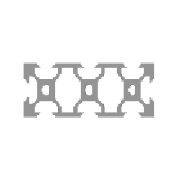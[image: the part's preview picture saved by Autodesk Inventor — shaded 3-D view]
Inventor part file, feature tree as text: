
AUTODESK INVENTOR PART (.ipt)
format: ipt  version: 2013 (Build 170138000, 138)  size: 249,344 bytes
history: native  units: mm
features: other x4, plane x3, split x2, sketch x2
ambient origin geometry x8: Origin, YZ Plane, XZ Plane, XY Plane, X Axis, Y Axis, Z Axis, Center Point
bodies: Solid1 (feature_tree), Body (feature_tree)
feature tree (11):
  other  "Driven Length"
  other  "Frame Generator"
  other  "Start Plane"
  other  "End Plane"
  plane  "Work Plane5"
  split  "Split1"
  plane  "Work Plane6"
  split  "Split2"
  sketch  "Sketch4"  dims[d0=10.0mm]
  plane  "Work Plane4"
  sketch  "Sketch5"  dims[d1=10.0mm d2=10.0mm d3=4.2mm d4=1.5mm d5=45.0deg d6=1.64mm d7=1.8mm d8=10.0mm d9=2.84mm d11=135.0deg d12=1.96mm d13=5.68mm d14=1.8mm d17=10.0mm d18=465.0mm d19=0.13mm d20=0.0mm d23=90.0deg d22=455.0mm]
